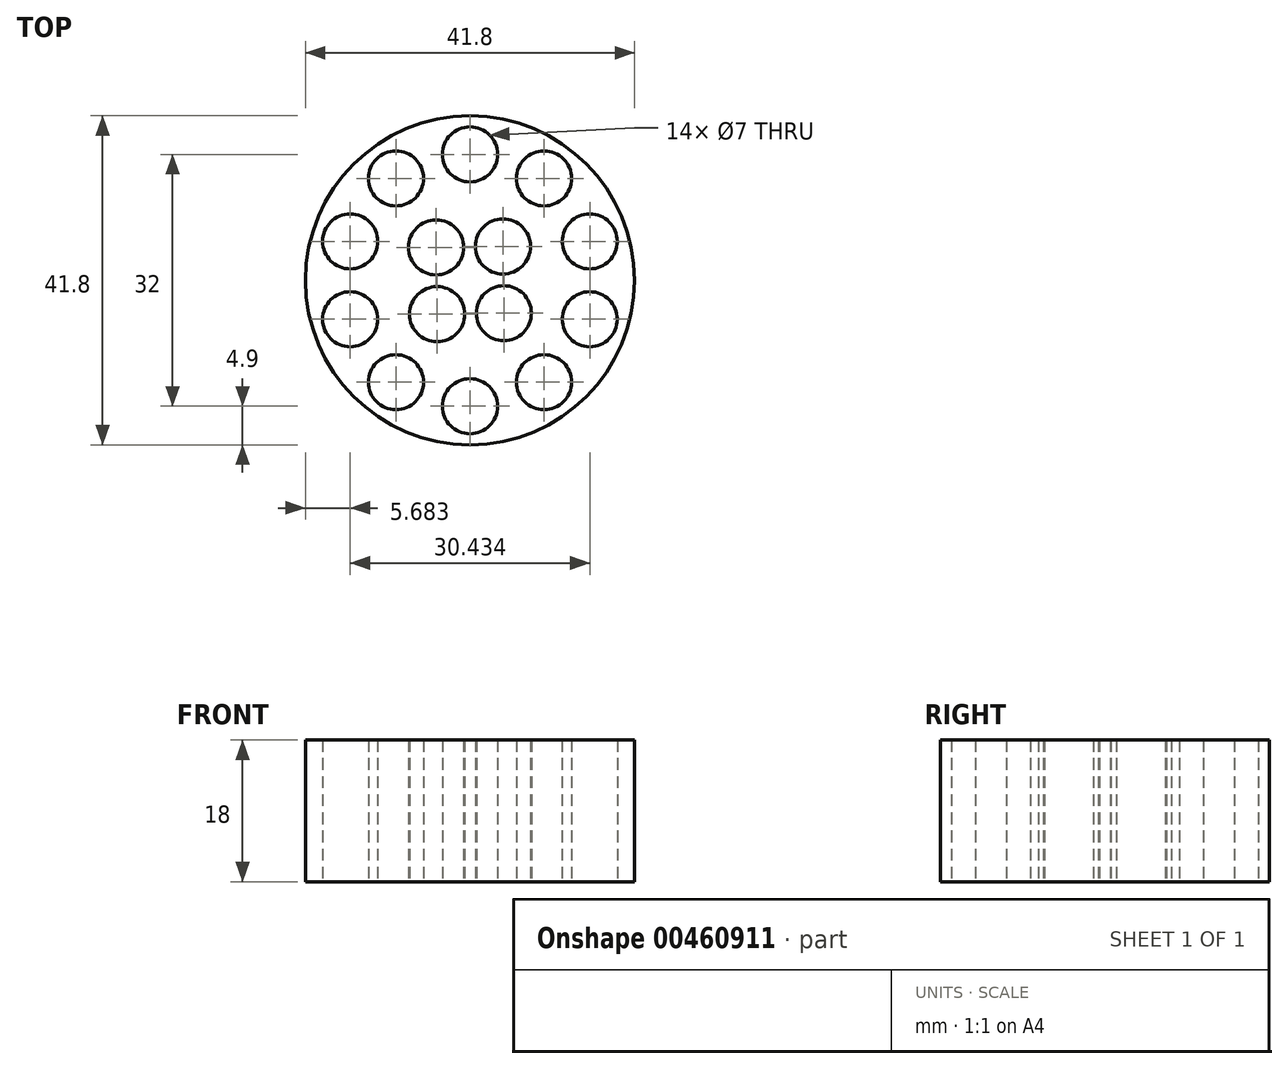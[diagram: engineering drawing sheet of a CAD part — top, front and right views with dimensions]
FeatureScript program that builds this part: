
annotation { "Feature Type Name" : "Feature", "Feature Type Description" : "" }
export const myFeature = defineFeature(function(context is Context, id is Id, definition is map)
    precondition{}
    {
        {
            var Q0;
            Q0=qCreatedBy(makeId("Top.planeOp"),FACE);
            var sketch = newSketch(context, id + "F0", { "sketchPlane" : qUnion([Q0])});
            skCircle(sketch, "E0", {"center": v(0, 0) * mm, "radius": 20.9 * mm});
            skCircle(sketch, "E1", {"center": v(0, 0) * mm, "radius": 6 * mm, "construction": true});
            skCircle(sketch, "E2", {"center": v(0, 0) * mm, "radius": 16 * mm, "construction": true});
            skCircle(sketch, "E3", {"center": v(0, 16) * mm, "radius": 3.5 * mm});
            skCircle(sketch, "E4", {"center": v(-4.3, 4.18) * mm, "radius": 3.5 * mm});
            skCircle(sketch, "E5.1.0", {"center": v(-9.4, 12.94) * mm, "radius": 3.5 * mm});
            skCircle(sketch, "E5.2.0", {"center": v(-15.22, 4.94) * mm, "radius": 3.5 * mm});
            skCircle(sketch, "E5.3.0", {"center": v(-15.22, -4.94) * mm, "radius": 3.5 * mm});
            skCircle(sketch, "E5.4.0", {"center": v(-9.4, -12.94) * mm, "radius": 3.5 * mm});
            skCircle(sketch, "E5.5.0", {"center": v(0, -16) * mm, "radius": 3.5 * mm});
            skCircle(sketch, "E5.6.0", {"center": v(9.4, -12.94) * mm, "radius": 3.5 * mm});
            skCircle(sketch, "E5.7.0", {"center": v(15.22, -4.94) * mm, "radius": 3.5 * mm});
            skCircle(sketch, "E5.8.0", {"center": v(15.22, 4.94) * mm, "radius": 3.5 * mm});
            skCircle(sketch, "E5.9.0", {"center": v(9.4, 12.94) * mm, "radius": 3.5 * mm});
            skCircle(sketch, "E6.1.0", {"center": v(-4.18, -4.3) * mm, "radius": 3.5 * mm});
            skCircle(sketch, "E6.2.0", {"center": v(4.3, -4.18) * mm, "radius": 3.5 * mm});
            skCircle(sketch, "E6.3.0", {"center": v(4.18, 4.3) * mm, "radius": 3.5 * mm});
            skSolve(sketch);
        }
        {
            var Q0;
            Q0=makeQuery(id+"F0.imprint","IMPRINT",FACE,{"disambiguationData":[TD([[makeQuery(id+"F0.imprint","IMPRINT",EDGE,{"derivedFrom":sQuery(id+"F0.wireOp",EDGE,"E0")}),1.0]])]});
            extrude(context, id + "F1", {"entities" : qUnion([Q0]), "depth" : 18 * mm, "offsetDistance" : 25 * mm});
        }
    });
